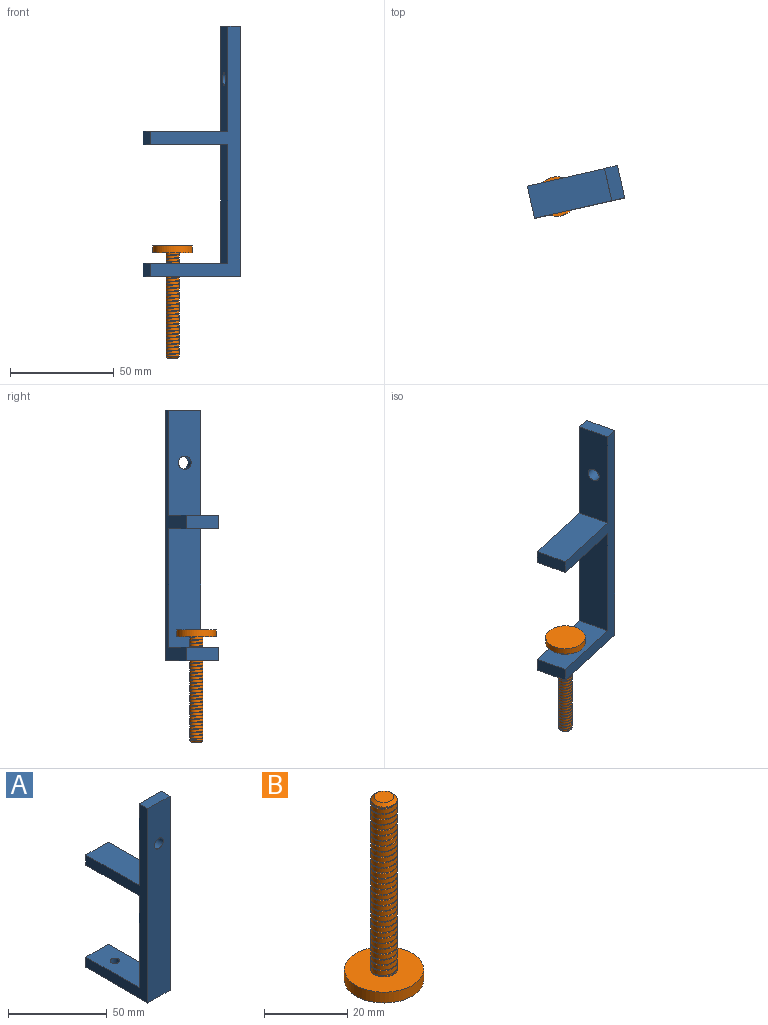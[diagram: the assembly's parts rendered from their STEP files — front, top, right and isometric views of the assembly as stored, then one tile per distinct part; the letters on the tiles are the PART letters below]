
ASSEMBLY  parts=2 mates=1
PART A: 14 faces, bbox 15.9x44.5x120.7 mm
  f0: plane 57.15x15.88mm, normal (0,1,0), area 907.3mm2, adj f1,f9,f10,f11
  f1: plane 38.1x15.88mm, normal (0,0,-1), area 604.8mm2, adj f0,f2,f10,f11
  f2: plane 15.88x6.35mm, normal (0,1,0), area 100.8mm2, adj f1,f3,f10,f11
  f3: plane 38.1x15.88mm, normal (0,0,1), area 604.8mm2, adj f2,f4,f10,f11
  f4: plane 50.8x15.88mm, normal (0,1,0), area 774.8mm2, adj f3,f5,f10,f11,f12
  f5: plane 15.88x6.35mm, normal (0,0,1), area 100.8mm2, adj f4,f6,f10,f11
  f6: plane 120.65x15.88mm, normal (0,-1,0), area 1883.6mm2, adj f5,f7,f10,f11,f12
  f7: plane 44.45x15.88mm, normal (0,0,-1), area 687.8mm2, adj f6,f8,f10,f11,f13
  f8: plane 15.88x6.35mm, normal (0,1,0), area 100.8mm2, adj f7,f9,f10,f11
  f9: plane 38.1x15.88mm, normal (0,0,1), area 587mm2, adj f0,f8,f10,f11,f13
  f10: plane 120.65x44.45mm, normal (1,0,0), area 1250mm2, adj f0,f1,f2,f3,f4,f5,f6,f7
  f11: plane 120.65x44.45mm, normal (-1,0,0), area 1250mm2, adj f0,f1,f2,f3,f4,f5,f6,f7
  f12: cylinder r=3.17mm len=6.35mm, axis (0,-1,0), area 126.7mm2, adj f4,f6
  f13: cylinder r=2.38mm len=6.35mm, axis (0,0,1), area 95mm2, adj f7,f9
PART B: 9 faces, bbox 19.1x19.1x54 mm
  f0: cylinder r=3.17mm len=50.01mm, axis (0,0,-1), area 991.7mm2, adj f4,f5,f6,f7,f8
  f1: plane 4.76x4.76mm, normal (0,0,1), area 17.8mm2, adj f5
  f2: cylinder r=9.53mm len=19.05mm, axis (0,0,1), area 190mm2, adj f3,f4
  f3: plane 19.05x19.05mm, normal (0,0,-1), area 285mm2, adj f2
  f4: plane 19.05x19.05mm, normal (0,0,1), area 253.4mm2, adj f0,f2
  f5: cone r=2.38mm half-angle=45deg, axis (0,0,-1), area 19.1mm2, adj f0,f1,f7,f8
  f6: plane 0.25x0.22mm, normal (0,-1,0), area 0mm2, adj f0,f7,f8
  f7: bspline ~50.39x7.33mm, area 153.8mm2, adj f0,f5,f6,f8
  f8: bspline ~50.39x7.33mm, area 154.5mm2, adj f0,f5,f6,f7
PLACE A rot(axis=(0,0,1),102.8deg) t=(31.94,27.71,41.16)mm fixed
PLACE B rot(axis=(0.99,-0.14,0),180deg) t=(2.52,21.04,-17.11)mm
MATE cylindrical B.f0 <-> A.f13  axis (0,0,-1) through (2.52,21.04,-67.91)mm
